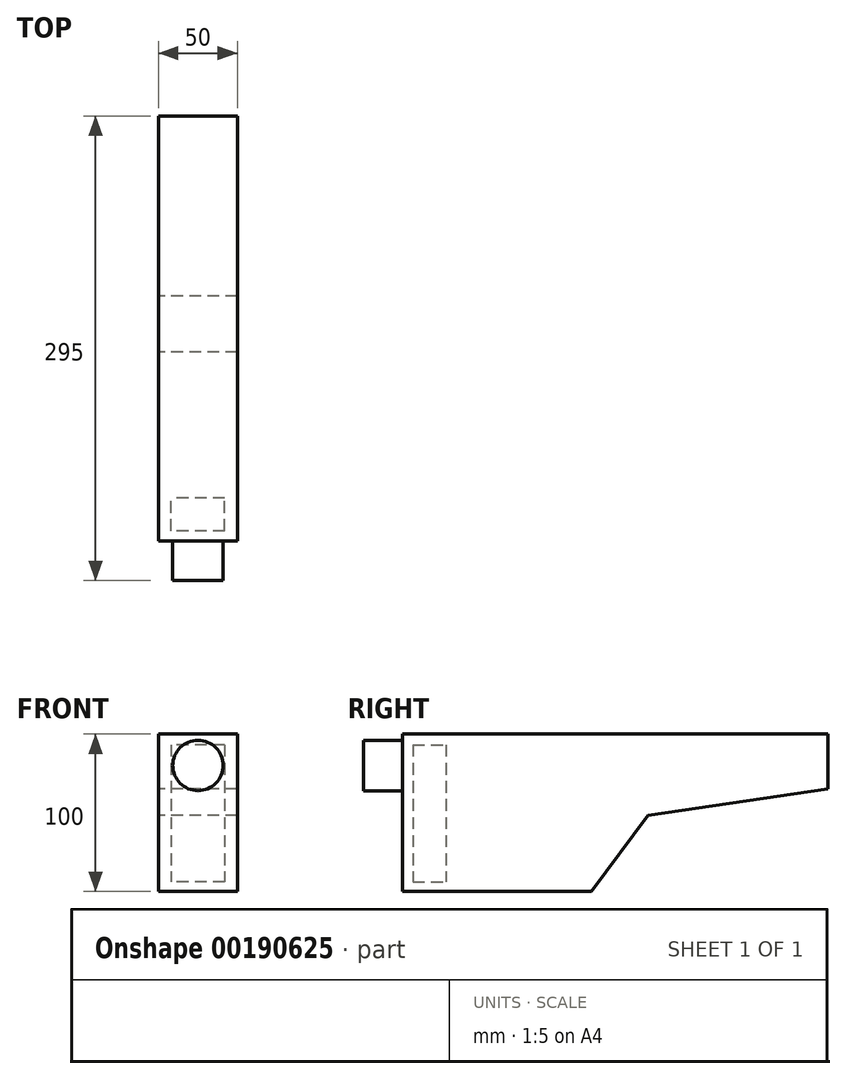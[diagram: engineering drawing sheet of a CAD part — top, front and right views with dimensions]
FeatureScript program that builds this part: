
annotation { "Feature Type Name" : "Feature", "Feature Type Description" : "" }
export const myFeature = defineFeature(function(context is Context, id is Id, definition is map)
    precondition{}
    {
        {
            var Q0;
            Q0=qCreatedBy(makeId("Right.planeOp"),FACE);
            var sketch = newSketch(context, id + "F0", { "sketchPlane" : qUnion([Q0])});
            skLineSegment(sketch, "E0", {"start": v(-304.8, 0) * mm, "end": v(304.8, 0) * mm, "construction": true});
            skSolve(sketch);
        }
        {
            var Q0;
            Q0=qCreatedBy(makeId("Right.planeOp"),FACE);
            var sketch = newSketch(context, id + "F1", { "sketchPlane" : qUnion([Q0])});
            skLineSegment(sketch, "E1", {"start": v(47.2, 0) * mm, "end": v(-222.8, 0) * mm});
            skLineSegment(sketch, "E2", {"start": v(-222.8, 0) * mm, "end": v(-222.8, -100) * mm});
            skLineSegment(sketch, "E3", {"start": v(-222.8, -100) * mm, "end": v(-102.8, -100) * mm});
            skLineSegment(sketch, "E4", {"start": v(-102.8, -100) * mm, "end": v(-67.02, -51.84) * mm});
            skLineSegment(sketch, "E5", {"start": v(47.2, -35) * mm, "end": v(47.2, 0) * mm});
            skLineSegment(sketch, "E6", {"start": v(-102.8, -100) * mm, "end": v(-102.8, 0) * mm, "construction": true});
            skLineSegment(sketch, "E7", {"start": v(-222.8, 0) * mm, "end": v(-254.8, 0) * mm, "construction": true});
            skLineSegment(sketch, "E8", {"start": v(-67.02, -51.84) * mm, "end": v(47.2, -35) * mm});
            skSolve(sketch);
        }
        {
            var Q0;
            Q0=qCreatedBy(makeId("Right.planeOp"),FACE);
            var sketch = newSketch(context, id + "F2", { "sketchPlane" : qUnion([Q0])});
            skLineSegment(sketch, "E9.bottom", {"start": v(-216.29, -6.85) * mm, "end": v(-195.29, -6.85) * mm});
            skLineSegment(sketch, "E9.top", {"start": v(-216.29, -93.85) * mm, "end": v(-195.29, -93.85) * mm});
            skLineSegment(sketch, "E9.left", {"start": v(-216.29, -6.85) * mm, "end": v(-216.29, -93.85) * mm});
            skLineSegment(sketch, "E9.right", {"start": v(-195.29, -6.85) * mm, "end": v(-195.29, -93.85) * mm});
            skSolve(sketch);
        }
        {
            var Q0;
            Q0=makeQuery(id+"F1.imprint","IMPRINT",FACE,{"disambiguationData":[TD([[makeQuery(id+"F1.imprint","IMPRINT",EDGE,{"derivedFrom":sQuery(id+"F1.wireOp",EDGE,"E1")}),1.0]])]});
            extrude(context, id + "F3", {"entities" : qUnion([Q0]), "endBound" : BoundingType.SYMMETRIC, "depth" : 50 * mm});
        }
        {
            var Q0;
            Q0 = qSketchRegion(id + "F2", true);
            extrude(context, id + "F4", {"entities" : qUnion([Q0]), "endBound" : BoundingType.SYMMETRIC, "depth" : 34 * mm});
        }
        {
            var Q0;
            Q0=makeQuery(id+"F3.opExtrude","SWEPT_FACE",FACE,{"disambiguationData":[OSD([sQuery(id+"F1.wireOp",EDGE,"E2")])]});
            var sketch = newSketch(context, id + "F5", { "sketchPlane" : qUnion([Q0])});
            skCircle(sketch, "E10", {"center": v(0, -20) * mm, "radius": 16 * mm});
            skSolve(sketch);
        }
        {
            var Q0;
            Q0 = qSketchRegion(id + "F5", true);
            extrude(context, id + "F6", {"entities" : qUnion([Q0]), "depth" : 25 * mm});
        }
    });
